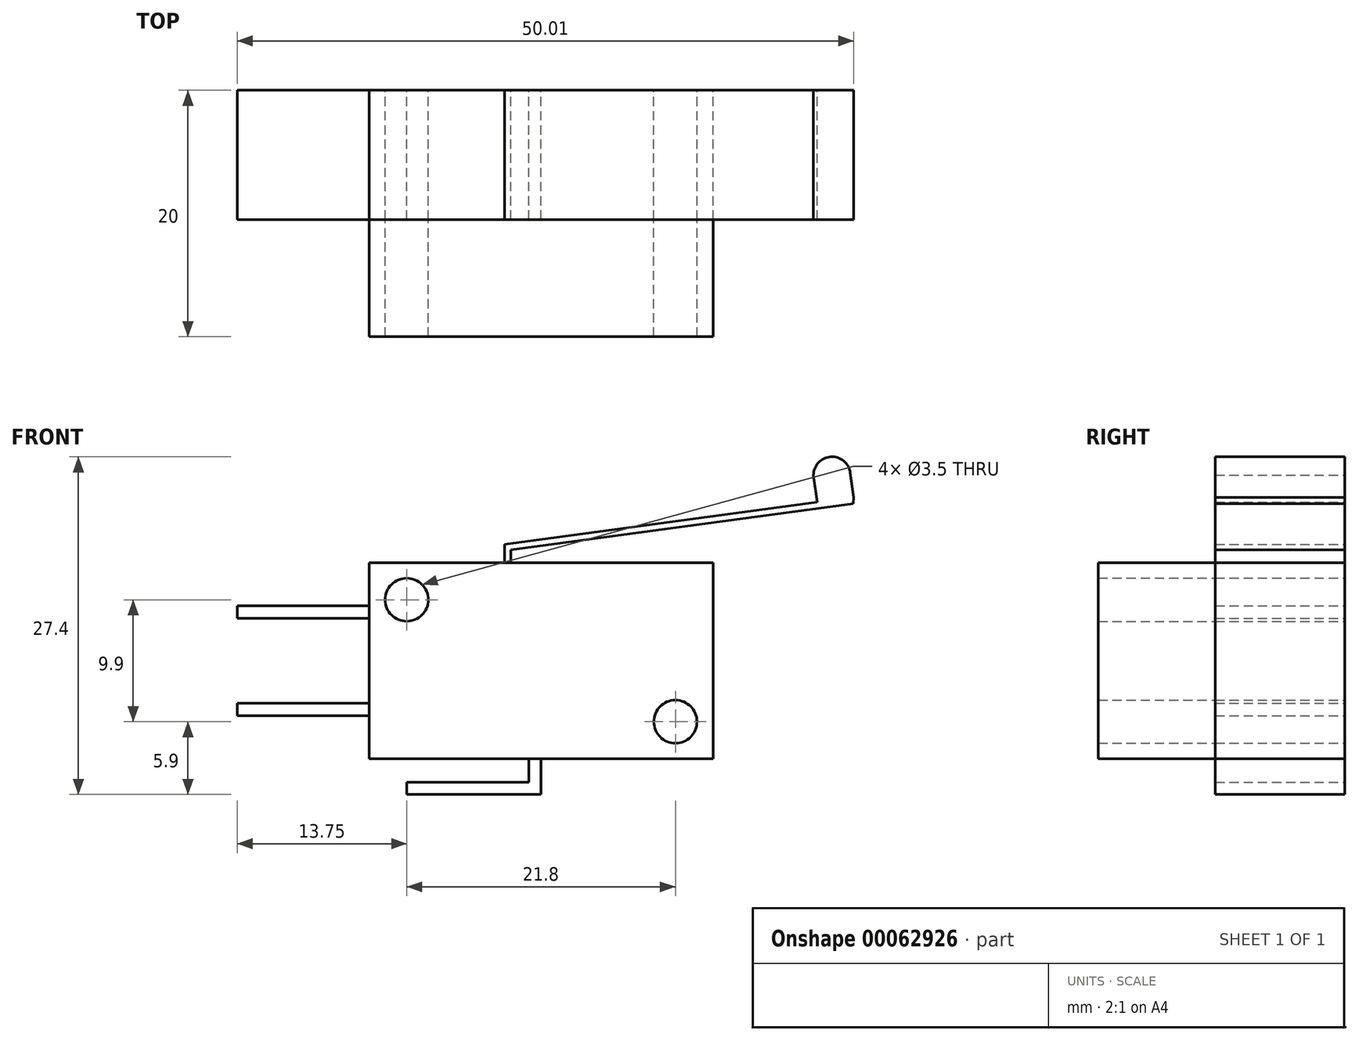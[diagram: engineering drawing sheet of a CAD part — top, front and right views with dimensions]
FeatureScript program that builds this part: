
annotation { "Feature Type Name" : "Feature", "Feature Type Description" : "" }
export const myFeature = defineFeature(function(context is Context, id is Id, definition is map)
    precondition{}
    {
        {
            var Q0;
            Q0=qCreatedBy(makeId("Front.planeOp"),FACE);
            var sketch = newSketch(context, id + "F0", { "sketchPlane" : qUnion([Q0])});
            skLineSegment(sketch, "E0.rect.top", {"start": v(13.95, -7.95) * mm, "end": v(0, -7.95) * mm});
            skLineSegment(sketch, "E0.rect.left", {"start": v(13.95, 7.95) * mm, "end": v(13.95, -7.95) * mm});
            skLineSegment(sketch, "E0.rect.right", {"start": v(-13.95, 7.95) * mm, "end": v(-13.95, 4.45) * mm});
            skPoint(sketch, "E0.rect.middle", {"position": v(0, 0) * mm});
            skCircle(sketch, "E1", {"center": v(-10.9, 4.95) * mm, "radius": 1.75 * mm});
            skCircle(sketch, "E2", {"center": v(10.9, -4.95) * mm, "radius": 1.75 * mm});
            skLineSegment(sketch, "E3", {"start": v(-10.9, 4.95) * mm, "end": v(10.9, -4.95) * mm, "construction": true});
            skLineSegment(sketch, "E4.bottom", {"start": v(-13.95, 4.45) * mm, "end": v(-24.65, 4.45) * mm});
            skLineSegment(sketch, "E4.top", {"start": v(-13.95, 3.45) * mm, "end": v(-24.65, 3.45) * mm});
            skLineSegment(sketch, "E4.right", {"start": v(-24.65, 4.45) * mm, "end": v(-24.65, 3.45) * mm});
            skLineSegment(sketch, "E5.bottom", {"start": v(-13.95, -3.45) * mm, "end": v(-24.65, -3.45) * mm});
            skLineSegment(sketch, "E5.top", {"start": v(-13.95, -4.45) * mm, "end": v(-24.65, -4.45) * mm});
            skLineSegment(sketch, "E5.right", {"start": v(-24.65, -3.45) * mm, "end": v(-24.65, -4.45) * mm});
            skLineSegment(sketch, "E6.top", {"start": v(0, -10.85) * mm, "end": v(-1, -10.85) * mm});
            skLineSegment(sketch, "E6.left", {"start": v(0, -7.95) * mm, "end": v(0, -10.85) * mm});
            skLineSegment(sketch, "E6.right", {"start": v(-1, -7.95) * mm, "end": v(-1, -9.85) * mm});
            skLineSegment(sketch, "E7.bottom", {"start": v(-1, -10.85) * mm, "end": v(-10.9, -10.85) * mm});
            skLineSegment(sketch, "E7.top", {"start": v(-1, -9.85) * mm, "end": v(-10.9, -9.85) * mm});
            skLineSegment(sketch, "E7.right", {"start": v(-10.9, -10.85) * mm, "end": v(-10.9, -9.85) * mm});
            skLineSegment(sketch, "E8.right", {"start": v(-2.95, 7.95) * mm, "end": v(-2.95, 9.45) * mm});
            skLineSegment(sketch, "E9", {"start": v(-2.95, 9.45) * mm, "end": v(22.4, 12.87) * mm});
            skLineSegment(sketch, "E10", {"start": v(25.32, 12.76) * mm, "end": v(25.36, 13.27) * mm});
            skLineSegment(sketch, "E11", {"start": v(25.36, 13.27) * mm, "end": v(25.09, 15.25) * mm});
            skArc(sketch, "E12", {"start": v(25.09, 15.25) * mm, "mid": v(23.5, 16.55) * mm, "end": v(22.1, 15.05) * mm});
            skLineSegment(sketch, "E13", {"start": v(22.1, 15.05) * mm, "end": v(22.4, 12.87) * mm});
            skLineSegment(sketch, "E14.trimOffspring", {"start": v(-13.95, -4.45) * mm, "end": v(-13.95, -7.95) * mm});
            skLineSegment(sketch, "E15.trimOffspring", {"start": v(-13.95, 3.45) * mm, "end": v(-13.95, -3.45) * mm});
            skLineSegment(sketch, "E16.trimOffspring", {"start": v(-1, -7.95) * mm, "end": v(-13.95, -7.95) * mm});
            skLineSegment(sketch, "E17.trimOffspring", {"start": v(-2.95, 7.95) * mm, "end": v(-13.95, 7.95) * mm});
            skLineSegment(sketch, "E18", {"start": v(25.32, 12.76) * mm, "end": v(-2.45, 9.01) * mm});
            skLineSegment(sketch, "E19", {"start": v(13.95, 7.95) * mm, "end": v(-2.45, 7.95) * mm});
            skLineSegment(sketch, "E20", {"start": v(-2.45, 7.95) * mm, "end": v(-2.45, 9.01) * mm});
            skSolve(sketch);
        }
        {
            var Q0;
            Q0 = qSketchRegion(id + "F0", true);
            extrude(context, id + "F1", {"entities" : qUnion([Q0]), "depth" : 10.5 * mm});
        }
        {
            var Q0;
            Q0=makeQuery(id+"F1.opExtrude","CAP_FACE",FACE,{"disambiguationData":[OSD([sQuery(id+"F0.wireOp",EDGE,"E0.rect.top"),sQuery(id+"F0.wireOp",EDGE,"E0.rect.left"),sQuery(id+"F0.wireOp",EDGE,"E0.rect.right"),sQuery(id+"F0.wireOp",EDGE,"E1"),sQuery(id+"F0.wireOp",EDGE,"E2"),sQuery(id+"F0.wireOp",EDGE,"E4.bottom"),sQuery(id+"F0.wireOp",EDGE,"E4.top"),sQuery(id+"F0.wireOp",EDGE,"E4.right"),sQuery(id+"F0.wireOp",EDGE,"E5.bottom"),sQuery(id+"F0.wireOp",EDGE,"E5.top"),sQuery(id+"F0.wireOp",EDGE,"E5.right"),sQuery(id+"F0.wireOp",EDGE,"E6.top"),sQuery(id+"F0.wireOp",EDGE,"E6.left"),sQuery(id+"F0.wireOp",EDGE,"E6.right"),sQuery(id+"F0.wireOp",EDGE,"E7.bottom"),sQuery(id+"F0.wireOp",EDGE,"E7.top"),sQuery(id+"F0.wireOp",EDGE,"E7.right"),sQuery(id+"F0.wireOp",EDGE,"E8.right"),sQuery(id+"F0.wireOp",EDGE,"E9"),sQuery(id+"F0.wireOp",EDGE,"E10"),sQuery(id+"F0.wireOp",EDGE,"E11"),sQuery(id+"F0.wireOp",EDGE,"E12"),sQuery(id+"F0.wireOp",EDGE,"E13"),sQuery(id+"F0.wireOp",EDGE,"E14.trimOffspring"),sQuery(id+"F0.wireOp",EDGE,"E15.trimOffspring"),sQuery(id+"F0.wireOp",EDGE,"E16.trimOffspring"),sQuery(id+"F0.wireOp",EDGE,"E17.trimOffspring"),sQuery(id+"F0.wireOp",EDGE,"E18"),sQuery(id+"F0.wireOp",EDGE,"E19"),sQuery(id+"F0.wireOp",EDGE,"E20")])],"isStart":false});
            var sketch = newSketch(context, id + "F2", { "sketchPlane" : qUnion([Q0])});
            skLineSegment(sketch, "E21.bottom", {"start": v(-13.95, 7.95) * mm, "end": v(13.95, 7.95) * mm});
            skLineSegment(sketch, "E21.top", {"start": v(-13.95, -7.95) * mm, "end": v(13.95, -7.95) * mm});
            skLineSegment(sketch, "E21.left", {"start": v(-13.95, 7.95) * mm, "end": v(-13.95, -7.95) * mm});
            skLineSegment(sketch, "E21.right", {"start": v(13.95, 7.95) * mm, "end": v(13.95, -7.95) * mm});
            skCircle(sketch, "E22", {"center": v(-10.9, 4.95) * mm, "radius": 1.75 * mm});
            skCircle(sketch, "E23", {"center": v(10.9, -4.95) * mm, "radius": 1.75 * mm});
            skSolve(sketch);
        }
        {
            var Q0;
            Q0 = qSketchRegion(id + "F2", true);
            extrude(context, id + "F3", {"entities" : qUnion([Q0]), "depth" : 9.5 * mm});
        }
    });
